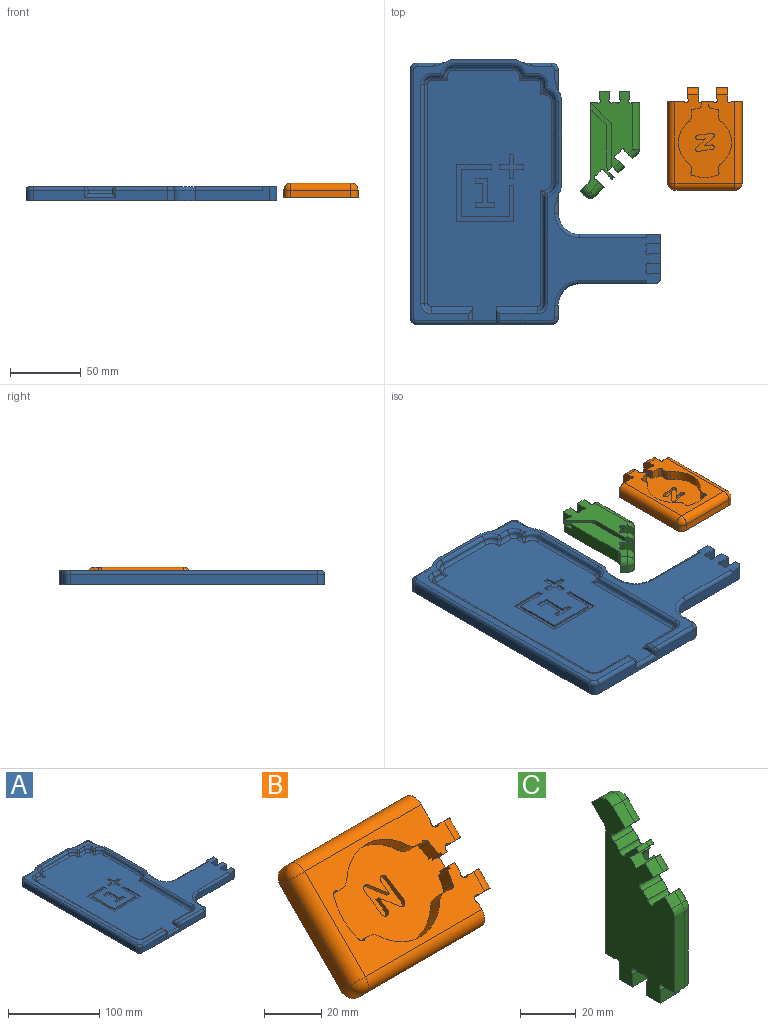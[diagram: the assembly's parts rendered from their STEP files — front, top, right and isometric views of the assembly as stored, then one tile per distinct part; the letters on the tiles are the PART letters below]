
ASSEMBLY  parts=3 mates=2
PART A: 154 faces, bbox 177.9x188.2x15 mm
  f0: plane 177.5x87.5mm, normal (0,0,1), area 13203.5mm2, adj f10,f11,f28,f29,f30,f31,f32,f33
  f1: plane 185x175mm, normal (0,0,1), area 4611.4mm2, adj f2,f3,f4,f5,f6,f7,f8,f9
  f2: plane 8x2.66mm, normal (1,0,0), area 21.3mm2, adj f1,f27,f116,f117
  f3: plane 8x7.83mm, normal (0,-1,0), area 62.6mm2, adj f1,f8,f27,f117
  f4: plane 8x7.83mm, normal (0,1,0), area 62.6mm2, adj f1,f8,f27,f116
  f5: plane 8x2.66mm, normal (1,0,0), area 21.3mm2, adj f1,f26,f114,f115
  f6: plane 8x7.83mm, normal (0,-1,0), area 62.6mm2, adj f1,f8,f26,f115
  f7: plane 8x7.83mm, normal (0,1,0), area 62.6mm2, adj f1,f8,f26,f114
  f8: plane 30x10mm, normal (1,0,0), area 185.6mm2, adj f1,f3,f4,f6,f7,f21,f25,f26
  f9: cylinder r=2.5mm len=47.5mm, axis (-1,0,0), area 186.5mm2, adj f1,f20,f80,f112
  f10: cylinder r=2.5mm len=80mm, axis (0,1,0), area 302.2mm2, adj f0,f12,f34,f60,f66
  f11: cylinder r=2.5mm len=12.5mm, axis (-1,0,0), area 37.2mm2, adj f0,f13,f38,f65,f73
  f12: cylinder r=2.5mm len=75.32mm, axis (0,-1,0), area 295.8mm2, adj f1,f10,f41,f67
  f13: cylinder r=2.5mm len=7.82mm, axis (1,0,0), area 30.7mm2, adj f1,f11,f43,f74
  f14: plane 13.49x7.5mm, normal (1,0,0), area 101.1mm2, adj f25,f95,f100,f106
  f15: plane 17.24x7.5mm, normal (0,1,0), area 129.3mm2, adj f25,f87,f102,f108
  f16: plane 95x7.5mm, normal (0,-1,0), area 602.5mm2, adj f25,f82,f84,f85,f86,f90,f96,f98
  f17: plane 175x7.5mm, normal (-1,0,0), area 1312.5mm2, adj f25,f89,f96,f102
  f18: plane 8.75x7.5mm, normal (1,0,0), area 65.6mm2, adj f19,f25,f81,f98
  f19: cylinder r=15mm len=15mm, axis (0,0,-1), area 176.7mm2, adj f18,f20,f25,f80
  f20: plane 52.5x10mm, normal (0,-1,0), area 406.2mm2, adj f1,f9,f19,f25,f112,f118
  f21: plane 57.5x10mm, normal (0,1,0), area 456.2mm2, adj f1,f8,f22,f25,f91,f113
  f22: cylinder r=15mm len=15mm, axis (0,0,-1), area 176.7mm2, adj f21,f23,f25,f92
  f23: plane 12.24x7.5mm, normal (1,0,0), area 91.8mm2, adj f22,f25,f93,f104
  f24: plane 18.49x7.5mm, normal (0,1,0), area 138.6mm2, adj f25,f94,f100,f110
  f25: plane 187.5x177.5mm, normal (0,0,-1), area 22331mm2, adj f8,f14,f15,f16,f17,f18,f19,f20
  f26: plane 10.54x8.08mm, normal (0,0,1), area 74.9mm2, adj f5,f6,f7,f8,f114,f115
  f27: plane 10.54x8.08mm, normal (0,0,1), area 74.9mm2, adj f2,f3,f4,f8,f116,f117
  f28: plane 10x2.5mm, normal (1,0,0), area 20.1mm2, adj f0,f30,f46,f86
  f29: plane 10x2.5mm, normal (-1,0,0), area 20.1mm2, adj f0,f32,f39,f84
  f30: cylinder r=2.5mm len=29mm, axis (1,0,0), area 113.9mm2, adj f0,f28,f31,f48
  f31: torus R=2.5mm, axis (0,0,1), area 25.2mm2, adj f0,f30,f33,f49
  f32: cylinder r=2.5mm len=29mm, axis (1,0,0), area 113.9mm2, adj f0,f29,f34,f40
  f33: cylinder r=2.5mm len=155mm, axis (0,-1,0), area 608.7mm2, adj f0,f31,f35,f47
  f34: torus R=2.5mm, axis (0,0,1), area 25.2mm2, adj f0,f10,f32,f41
  f35: torus R=2.5mm, axis (0,0,1), area 25.2mm2, adj f0,f33,f37,f45
  f36: cylinder r=2.5mm len=7.5mm, axis (0,1,0), area 17.5mm2, adj f0,f38,f42,f56,f71
  f37: cylinder r=2.5mm len=11.25mm, axis (-1,0,0), area 32.3mm2, adj f0,f35,f44,f61,f78
  f38: torus R=2.5mm, axis (0,0,1), area 25.2mm2, adj f0,f11,f36,f43
  f39: cylinder r=2.5mm len=7.5mm, axis (0,-1,0), area 24.5mm2, adj f1,f29,f40,f83
  f40: cylinder r=2.5mm len=29mm, axis (-1,0,0), area 109mm2, adj f1,f32,f39,f41
  f41: torus R=7.5mm, axis (0,0,1), area 36.4mm2, adj f1,f12,f34,f40
  f42: cylinder r=2.5mm len=2.82mm, axis (0,-1,0), area 11.1mm2, adj f1,f36,f43,f72
  f43: torus R=7.5mm, axis (0,0,1), area 36.4mm2, adj f1,f13,f38,f42
  f44: cylinder r=2.5mm len=6.57mm, axis (1,0,0), area 25.8mm2, adj f1,f37,f45,f79
  f45: torus R=7.5mm, axis (0,0,1), area 36.4mm2, adj f1,f35,f44,f47
  f46: cylinder r=2.5mm len=7.5mm, axis (0,1,0), area 24.5mm2, adj f1,f28,f48,f88
  f47: cylinder r=2.5mm len=155mm, axis (0,1,0), area 608.7mm2, adj f1,f33,f45,f49
  f48: cylinder r=2.5mm len=29mm, axis (-1,0,0), area 109mm2, adj f1,f30,f46,f49
  f49: torus R=7.5mm, axis (0,0,1), area 36.4mm2, adj f1,f31,f47,f48
  f50: cylinder r=12.5mm len=10mm, axis (0,0,1), area 68.4mm2, adj f1,f25,f51,f108,f109
  f51: plane 41.25x10mm, normal (0,1,0), area 412.5mm2, adj f1,f25,f50,f52
  f52: cylinder r=12.5mm len=10mm, axis (0,0,1), area 68.4mm2, adj f1,f25,f51,f110,f111
  f53: plane 57.5x10mm, normal (1,0,0), area 575mm2, adj f1,f25,f54,f55
  f54: cylinder r=12.5mm len=10mm, axis (0,0,1), area 68.4mm2, adj f1,f25,f53,f104,f105
  f55: cylinder r=12.5mm len=10mm, axis (0,0,1), area 68.4mm2, adj f1,f25,f53,f106,f107
  f56: cylinder r=2.5mm len=2.5mm, axis (1,0,0), area 1.8mm2, adj f0,f36,f57,f71
  f57: torus R=5mm, axis (0,0,1), area 38.3mm2, adj f0,f56,f58,f70,f71
  f58: cylinder r=2.5mm len=57.5mm, axis (0,-1,0), area 225.8mm2, adj f0,f57,f59,f69
  f59: torus R=5mm, axis (0,0,1), area 38.3mm2, adj f0,f58,f60,f66,f68
  f60: cylinder r=2.5mm len=2.5mm, axis (-1,0,0), area 1.8mm2, adj f0,f10,f59,f66
  f61: cylinder r=2.5mm len=2.5mm, axis (0,1,0), area 1.8mm2, adj f0,f37,f62,f78
  f62: torus R=5mm, axis (0,0,1), area 38.3mm2, adj f0,f61,f63,f77,f78
  f63: cylinder r=2.5mm len=41.25mm, axis (1,0,0), area 162mm2, adj f0,f62,f64,f76
  f64: torus R=5mm, axis (0,0,1), area 38.3mm2, adj f0,f63,f65,f73,f75
  f65: cylinder r=2.5mm len=2.5mm, axis (0,-1,0), area 1.8mm2, adj f0,f11,f64,f73
  f66: bspline ~4.92x4.19mm, area 9.5mm2, adj f10,f59,f60,f67
  f67: sphere r=2.5mm, area 12.2mm2, adj f12,f66,f68
  f68: torus R=10mm, axis (0,0,1), area 43.5mm2, adj f1,f59,f67,f69
  f69: cylinder r=2.5mm len=57.5mm, axis (0,-1,0), area 225.8mm2, adj f1,f58,f68,f70
  f70: torus R=10mm, axis (0,0,1), area 43.5mm2, adj f1,f57,f69,f72
  f71: bspline ~4.92x4.19mm, area 9.5mm2, adj f36,f56,f57,f72
  f72: sphere r=2.5mm, area 12.2mm2, adj f42,f70,f71
  f73: bspline ~4.92x4.19mm, area 9.5mm2, adj f11,f64,f65,f74
  f74: sphere r=2.5mm, area 12.2mm2, adj f13,f73,f75
  f75: torus R=10mm, axis (0,0,1), area 43.5mm2, adj f1,f64,f74,f76
  f76: cylinder r=2.5mm len=41.25mm, axis (1,0,0), area 162mm2, adj f1,f63,f75,f77
  f77: torus R=10mm, axis (0,0,1), area 43.5mm2, adj f1,f62,f76,f79
  f78: bspline ~4.92x4.19mm, area 9.5mm2, adj f37,f61,f62,f79
  f79: sphere r=2.5mm, area 12.2mm2, adj f44,f77,f78
  f80: torus R=17.5mm, axis (0,0,1), area 98.1mm2, adj f1,f9,f19,f81
  f81: cylinder r=2.5mm len=8.75mm, axis (0,-1,0), area 34.4mm2, adj f1,f18,f80,f99
  f82: cylinder r=2.5mm len=36.5mm, axis (-1,0,0), area 143.3mm2, adj f1,f16,f83,f99
  f83: sphere r=2.5mm, area 9.8mm2, adj f39,f82,f84
  f84: cylinder r=2.5mm len=5mm, axis (0,0,1), area 14.7mm2, adj f16,f29,f83,f85
  f85: cylinder r=2.5mm len=22mm, axis (-1,0,0), area 76.6mm2, adj f0,f16,f84,f86
  f86: cylinder r=2.5mm len=5mm, axis (0,0,-1), area 14.7mm2, adj f16,f28,f85,f88
  f87: cylinder r=2.5mm len=17.24mm, axis (1,0,0), area 54.3mm2, adj f1,f15,f103,f109
  f88: sphere r=2.5mm, area 13.4mm2, adj f46,f86,f90
  f89: cylinder r=2.5mm len=175mm, axis (0,1,0), area 687.2mm2, adj f1,f17,f97,f103
  f90: cylinder r=2.5mm len=36.5mm, axis (-1,0,0), area 143.3mm2, adj f1,f16,f88,f97
  f91: cylinder r=2.5mm len=47.5mm, axis (1,0,0), area 186.5mm2, adj f1,f21,f92,f113
  f92: torus R=17.5mm, axis (0,0,1), area 98.1mm2, adj f1,f22,f91,f93
  f93: cylinder r=2.5mm len=12.24mm, axis (0,-1,0), area 34.7mm2, adj f1,f23,f92,f105
  f94: cylinder r=2.5mm len=18.49mm, axis (1,0,0), area 59.2mm2, adj f1,f24,f101,f111
  f95: cylinder r=2.5mm len=13.49mm, axis (0,-1,0), area 39.6mm2, adj f1,f14,f101,f107
  f96: cylinder r=5mm len=7.5mm, axis (0,0,-1), area 58.9mm2, adj f16,f17,f25,f97
  f97: torus R=2.5mm, axis (0,0,1), area 25.2mm2, adj f1,f89,f90,f96
  f98: cylinder r=5mm len=7.5mm, axis (0,0,1), area 58.9mm2, adj f16,f18,f25,f99
  f99: torus R=2.5mm, axis (0,0,1), area 25.2mm2, adj f1,f81,f82,f98
  f100: cylinder r=5mm len=7.5mm, axis (0,0,-1), area 58.9mm2, adj f14,f24,f25,f101
  f101: torus R=2.5mm, axis (0,0,1), area 25.2mm2, adj f1,f94,f95,f100
  f102: cylinder r=5mm len=7.5mm, axis (0,0,1), area 58.9mm2, adj f15,f17,f25,f103
  f103: torus R=2.5mm, axis (0,0,1), area 25.2mm2, adj f1,f87,f89,f102
  f104: cylinder r=5mm len=7.5mm, axis (0,0,1), area 20.3mm2, adj f23,f25,f54,f105
  f105: bspline ~9.82x7.96mm, area 13.2mm2, adj f1,f54,f93,f104
  f106: cylinder r=5mm len=7.5mm, axis (0,0,1), area 20.3mm2, adj f14,f25,f55,f107
  f107: bspline ~9.82x7.96mm, area 13.2mm2, adj f1,f55,f95,f106
  f108: cylinder r=5mm len=7.5mm, axis (0,0,1), area 20.3mm2, adj f15,f25,f50,f109
  f109: bspline ~9.82x7.96mm, area 13.2mm2, adj f1,f50,f87,f108
  f110: cylinder r=5mm len=7.5mm, axis (0,0,1), area 20.3mm2, adj f24,f25,f52,f111
  f111: bspline ~9.82x7.96mm, area 13.2mm2, adj f1,f52,f94,f110
  f112: plane 2.5x2.5mm, normal (-1,0,0), area 1.3mm2, adj f1,f9,f20
  f113: plane 2.5x2.5mm, normal (-1,0,0), area 1.3mm2, adj f1,f21,f91
  f114: cylinder r=1.59mm len=8mm, axis (0,0,-1), area 39.9mm2, adj f1,f5,f7,f26
  f115: cylinder r=1.59mm len=8mm, axis (0,0,-1), area 39.9mm2, adj f1,f5,f6,f26
  f116: cylinder r=1.59mm len=8mm, axis (0,0,-1), area 39.9mm2, adj f1,f2,f4,f27
  f117: cylinder r=1.59mm len=8mm, axis (0,0,-1), area 39.9mm2, adj f1,f2,f3,f27
  f118: cylinder r=5mm len=10mm, axis (0,0,-1), area 78.5mm2, adj f1,f8,f20,f25
  f119: plane 24.75x1.5mm, normal (0,-1,0), area 37.1mm2, adj f0,f120,f128,f129
  f120: plane 40.5x1.5mm, normal (1,0,0), area 60.8mm2, adj f0,f119,f121,f129
  f121: plane 40.5x1.5mm, normal (0,1,0), area 60.7mm2, adj f0,f120,f122,f129
  f122: plane 25.31x1.5mm, normal (-1,0,0), area 38mm2, adj f0,f121,f123,f129
  f123: plane 3.38x1.5mm, normal (0,-1,0), area 5.1mm2, adj f0,f122,f124,f129
  f124: plane 21.94x1.5mm, normal (1,0,0), area 32.9mm2, adj f0,f123,f125,f129
  f125: plane 33.75x1.5mm, normal (0,-1,0), area 50.6mm2, adj f0,f124,f126,f129
  f126: plane 33.75x1.5mm, normal (-1,0,0), area 50.6mm2, adj f0,f125,f127,f129
  f127: plane 21.38x1.5mm, normal (0,1,0), area 32.1mm2, adj f0,f126,f128,f129
  f128: plane 3.38x1.5mm, normal (-1,0,0), area 5.1mm2, adj f0,f119,f127,f129
  f129: plane 40.5x40.5mm, normal (0,0,1), area 408.2mm2, adj f119,f120,f121,f122,f123,f124,f125,f126
  f130: plane 8.44x1.5mm, normal (0,-1,0), area 12.7mm2, adj f0,f131,f139,f140
  f131: plane 3.38x1.5mm, normal (1,0,0), area 5.1mm2, adj f0,f130,f132,f140
  f132: plane 5.06x1.5mm, normal (0,1,0), area 7.6mm2, adj f0,f131,f133,f140
  f133: plane 13.5x1.5mm, normal (1,0,0), area 20.3mm2, adj f0,f132,f134,f140
  f134: plane 5.06x1.5mm, normal (0,-1,0), area 7.6mm2, adj f0,f133,f135,f140
  f135: plane 3.38x1.5mm, normal (1,0,0), area 5.1mm2, adj f0,f134,f136,f140
  f136: plane 13.5x1.5mm, normal (0,1,0), area 20.3mm2, adj f0,f135,f137,f140
  f137: plane 3.38x1.5mm, normal (-1,0,0), area 5.1mm2, adj f0,f136,f138,f140
  f138: plane 5.06x1.5mm, normal (0,-1,0), area 7.6mm2, adj f0,f137,f139,f140
  f139: plane 16.88x1.5mm, normal (-1,0,0), area 25.3mm2, adj f0,f130,f138,f140
  f140: plane 20.25x13.5mm, normal (0,0,1), area 119.6mm2, adj f130,f131,f132,f133,f134,f135,f136,f137
  f141: plane 6.75x1.5mm, normal (-1,0,0), area 10.1mm2, adj f0,f142,f152,f153
  f142: plane 3.38x1.5mm, normal (0,-1,0), area 5.1mm2, adj f0,f141,f143,f153
  f143: plane 6.75x1.5mm, normal (1,0,0), area 10.1mm2, adj f0,f142,f144,f153
  f144: plane 6.75x1.5mm, normal (0,-1,0), area 10.1mm2, adj f0,f143,f145,f153
  f145: plane 3.38x1.5mm, normal (1,0,0), area 5.1mm2, adj f0,f144,f146,f153
  f146: plane 6.75x1.5mm, normal (0,1,0), area 10.1mm2, adj f0,f145,f147,f153
  f147: plane 6.75x1.5mm, normal (1,0,0), area 10.1mm2, adj f0,f146,f148,f153
  f148: plane 3.38x1.5mm, normal (0,1,0), area 5.1mm2, adj f0,f147,f149,f153
  f149: plane 6.75x1.5mm, normal (-1,0,0), area 10.1mm2, adj f0,f148,f150,f153
  f150: plane 6.75x1.5mm, normal (0,1,0), area 10.1mm2, adj f0,f149,f151,f153
  f151: plane 3.38x1.5mm, normal (-1,0,0), area 5.1mm2, adj f0,f150,f152,f153
  f152: plane 6.75x1.5mm, normal (0,-1,0), area 10.1mm2, adj f0,f141,f151,f153
  f153: plane 16.88x16.88mm, normal (0,0,1), area 102.5mm2, adj f141,f142,f143,f144,f145,f146,f147,f148
PART B: 62 faces, bbox 72.5x42.1x42.1 mm
  f0: plane 62.5x30mm, normal (0,-0.71,0.71), area 1144.2mm2, adj f1,f2,f3,f4,f5,f6,f7,f8
  f1: plane 4.6x4.6mm, normal (0,0.71,0.71), area 13.7mm2, adj f0,f31,f40,f50
  f2: cylinder r=24.75mm len=7.91mm, axis (0,-0.71,0.71), area 31.3mm2, adj f0,f31,f41,f50
  f3: cylinder r=24.75mm len=16.33mm, axis (0,-0.71,0.71), area 110mm2, adj f0,f31,f48,f49
  f4: plane 4.6x4.6mm, normal (0,0.71,0.71), area 11.7mm2, adj f0,f31,f38,f49
  f5: plane 4.6x4.6mm, normal (0,-0.71,-0.71), area 11.7mm2, adj f0,f31,f37,f48
  f6: cylinder r=24.75mm len=7.91mm, axis (0,-0.71,0.71), area 31.3mm2, adj f0,f31,f34,f47
  f7: plane 4.6x4.6mm, normal (0,-0.71,-0.71), area 13.7mm2, adj f0,f31,f35,f47
  f8: plane 12.56x10.48mm, normal (1,0,0), area 72.2mm2, adj f0,f16,f22,f23,f46
  f9: plane 7.76x7.07mm, normal (0,-0.71,-0.71), area 72.2mm2, adj f0,f16,f17,f30,f46
  f10: plane 12.84x9.81mm, normal (1,0,0), area 53.7mm2, adj f0,f16,f31,f32,f44,f45
  f11: plane 7.76x7.07mm, normal (0,0.71,0.71), area 72.2mm2, adj f0,f16,f17,f30,f45
  f12: plane 4.6x4.6mm, normal (0,-0.71,-0.71), area 18.4mm2, adj f0,f31,f33,f44
  f13: plane 7.76x7.07mm, normal (0,-0.71,-0.71), area 72.2mm2, adj f0,f16,f18,f29,f44
  f14: plane 15.44x13.37mm, normal (1,0,0), area 112.9mm2, adj f0,f16,f19,f21,f43
  f15: plane 7.76x7.07mm, normal (0,0.71,0.71), area 72.2mm2, adj f0,f16,f18,f29,f43
  f16: plane 72.5x37.07mm, normal (0,0.71,-0.71), area 3417.2mm2, adj f8,f9,f10,f11,f13,f14,f15,f17
  f17: plane 9.09x9.09mm, normal (1,0,0), area 39.2mm2, adj f9,f11,f16,f30
  f18: plane 9.09x9.09mm, normal (1,0,0), area 39.2mm2, adj f13,f15,f16,f29
  f19: plane 57.5x3.54mm, normal (0,0.71,0.71), area 287.5mm2, adj f14,f16,f21,f28
  f20: plane 33.54x33.54mm, normal (-1,0,0), area 212.1mm2, adj f16,f24,f26,f28
  f21: cylinder r=5mm len=57.5mm, axis (-1,0,0), area 451.6mm2, adj f0,f14,f19,f27
  f22: plane 57.5x3.54mm, normal (0,-0.71,-0.71), area 287.5mm2, adj f8,f16,f23,f24
  f23: cylinder r=5mm len=57.5mm, axis (1,0,0), area 451.6mm2, adj f0,f8,f22,f25
  f24: cylinder r=5mm len=7.07mm, axis (0,0.71,-0.71), area 39.3mm2, adj f16,f20,f22,f25
  f25: sphere r=5mm, area 39.3mm2, adj f23,f24,f26
  f26: cylinder r=5mm len=33.54mm, axis (0,-0.71,-0.71), area 333.2mm2, adj f0,f20,f25,f27
  f27: sphere r=5mm, area 39.3mm2, adj f21,f26,f28
  f28: cylinder r=5mm len=7.07mm, axis (0,-0.71,0.71), area 39.3mm2, adj f16,f19,f20,f27
  f29: cylinder r=5mm len=9.09mm, axis (0,0.71,0.71), area 61.7mm2, adj f0,f13,f15,f18
  f30: cylinder r=5mm len=9.09mm, axis (0,0.71,0.71), area 61.7mm2, adj f0,f9,f11,f17
  f31: plane 53.5x26.52mm, normal (0,-0.71,0.71), area 1261.3mm2, adj f1,f2,f3,f4,f5,f6,f7,f10
  f32: plane 4.6x4.6mm, normal (0,0.71,0.71), area 19.5mm2, adj f0,f10,f31,f42
  f33: plane 5.3x5.3mm, normal (-1,0,0), area 6.5mm2, adj f0,f12,f31,f34
  f34: plane 4.6x4.6mm, normal (0,-0.71,-0.71), area 7.9mm2, adj f0,f6,f31,f33
  f35: cylinder r=5mm len=5.97mm, axis (0,-0.71,0.71), area 29.7mm2, adj f0,f7,f31,f36
  f36: cylinder r=18.75mm len=29.7mm, axis (0,-0.71,0.71), area 222.8mm2, adj f0,f31,f35,f37
  f37: cylinder r=5mm len=5.97mm, axis (0,-0.71,0.71), area 29.7mm2, adj f0,f5,f31,f36
  f38: cylinder r=5mm len=5.97mm, axis (0,-0.71,0.71), area 29.7mm2, adj f0,f4,f31,f39
  f39: cylinder r=18.75mm len=29.7mm, axis (0,-0.71,0.71), area 222.8mm2, adj f0,f31,f38,f40
  f40: cylinder r=5mm len=5.97mm, axis (0,-0.71,0.71), area 29.7mm2, adj f0,f1,f31,f39
  f41: plane 4.6x4.6mm, normal (0,0.71,0.71), area 7.9mm2, adj f0,f2,f31,f42
  f42: plane 5.3x5.3mm, normal (-1,0,0), area 6.5mm2, adj f0,f31,f32,f41
  f43: cylinder r=1.59mm len=8.99mm, axis (0,0.71,-0.71), area 49.9mm2, adj f0,f14,f15,f16
  f44: cylinder r=1.59mm len=8.99mm, axis (0,0.71,-0.71), area 48.1mm2, adj f0,f10,f12,f13,f16,f31
  f45: cylinder r=1.59mm len=8.99mm, axis (0,0.71,-0.71), area 49.9mm2, adj f0,f10,f11,f16
  f46: cylinder r=1.59mm len=8.99mm, axis (0,0.71,-0.71), area 49.9mm2, adj f0,f8,f9,f16
  f47: cylinder r=1.59mm len=5.94mm, axis (0,0.71,-0.71), area 25mm2, adj f0,f6,f7,f31
  f48: cylinder r=1.59mm len=5.77mm, axis (0,0.71,-0.71), area 24.8mm2, adj f0,f3,f5,f31
  f49: cylinder r=1.59mm len=5.77mm, axis (0,0.71,-0.71), area 24.8mm2, adj f0,f3,f4,f31
  f50: cylinder r=1.59mm len=5.94mm, axis (0,0.71,-0.71), area 25mm2, adj f0,f1,f2,f31
  f51: plane 4.97x4.97mm, normal (0.99,0.1,0.1), area 10.2mm2, adj f31,f52,f60,f61
  f52: plane 6.14x5.91mm, normal (-0.72,-0.49,-0.49), area 17.7mm2, adj f31,f51,f53,f61
  f53: cylinder r=1.6mm len=2.75mm, axis (0,-0.71,0.71), area 8mm2, adj f31,f52,f54,f61
  f54: plane 8.42x8.42mm, normal (0.99,0.1,0.1), area 20mm2, adj f31,f53,f55,f61
  f55: cylinder r=1.6mm len=3.18mm, axis (0,-0.71,0.71), area 10.1mm2, adj f31,f54,f56,f61
  f56: plane 4.97x4.97mm, normal (-0.99,-0.1,-0.1), area 10.2mm2, adj f31,f55,f57,f61
  f57: plane 6.14x5.91mm, normal (0.72,0.49,0.49), area 17.7mm2, adj f31,f56,f58,f61
  f58: cylinder r=1.6mm len=2.75mm, axis (0,-0.71,0.71), area 8mm2, adj f31,f57,f59,f61
  f59: plane 8.42x8.42mm, normal (-0.99,-0.1,-0.1), area 20mm2, adj f31,f58,f60,f61
  f60: cylinder r=1.6mm len=3.18mm, axis (0,-0.71,0.71), area 10.1mm2, adj f31,f51,f59,f61
  f61: plane 12.76x9.27mm, normal (0,-0.71,0.71), area 106.8mm2, adj f51,f52,f53,f54,f55,f56,f57,f58
PART C: 57 faces, bbox 10x42.1x75.9 mm
  f0: plane 5x4.22mm, normal (0,-0.71,0.71), area 29.8mm2, adj f3,f4,f14,f37
  f1: plane 54.34x30mm, normal (1,0,0), area 774.9mm2, adj f3,f5,f6,f7,f8,f9,f10,f11
  f2: plane 56.99x16.94mm, normal (1,0,0), area 523.7mm2, adj f15,f16,f17,f22,f24,f28,f30,f32
  f3: cylinder r=5mm len=7.75mm, axis (0,-0.71,-0.71), area 46.8mm2, adj f0,f1,f14,f37
  f4: plane 75.93x42.07mm, normal (-1,0,0), area 1788mm2, adj f0,f5,f6,f7,f8,f9,f10,f11
  f5: plane 10x4.58mm, normal (0,0,-1), area 45.8mm2, adj f1,f4,f24,f42,f56
  f6: plane 10x5.76mm, normal (0,1,0), area 57.5mm2, adj f1,f4,f20,f56
  f7: plane 10x2.66mm, normal (0,0,-1), area 26.6mm2, adj f1,f4,f54,f55
  f8: plane 10x5.76mm, normal (0,-1,0), area 57.5mm2, adj f1,f4,f20,f55
  f9: plane 10x5.76mm, normal (0,1,0), area 57.5mm2, adj f1,f4,f19,f54
  f10: plane 10x5.08mm, normal (0,0,-1), area 45.4mm2, adj f1,f4,f23,f35,f53
  f11: plane 10x5.76mm, normal (0,-1,0), area 57.5mm2, adj f1,f4,f19,f53
  f12: plane 10x2.59mm, normal (0,-0.71,0.71), area 36.6mm2, adj f1,f4,f51,f52
  f13: plane 10x5.48mm, normal (0,0.71,0.71), area 72.2mm2, adj f1,f4,f25,f33,f52
  f14: plane 10x5.48mm, normal (0,-0.71,-0.71), area 72.2mm2, adj f0,f1,f3,f4,f51
  f15: plane 10x2.59mm, normal (0,-0.71,0.71), area 36.6mm2, adj f2,f4,f49,f50
  f16: plane 10x5.48mm, normal (0,0.71,0.71), area 72.2mm2, adj f2,f4,f21,f22,f50
  f17: plane 10x5.48mm, normal (0,-0.71,-0.71), area 72.2mm2, adj f2,f4,f18,f30,f49
  f18: plane 6.31x6.31mm, normal (0,-0.71,0.71), area 44.6mm2, adj f4,f17,f27,f30
  f19: plane 10x6.85mm, normal (0,0,-1), area 68.5mm2, adj f1,f4,f9,f11
  f20: plane 10x6.85mm, normal (0,0,-1), area 68.5mm2, adj f1,f4,f6,f8
  f21: plane 5x1.34mm, normal (0,-0.71,0.71), area 9.4mm2, adj f4,f16,f22,f38
  f22: cylinder r=5mm len=5mm, axis (0,-0.71,-0.71), area 14.8mm2, adj f2,f16,f21,f38
  f23: plane 32.93x5mm, normal (0,-1,0), area 164.6mm2, adj f4,f10,f26,f35
  f24: plane 53.79x10mm, normal (0,1,0), area 506.6mm2, adj f2,f4,f5,f36,f43,f48
  f25: plane 5x3.43mm, normal (0,-0.71,0.71), area 24.3mm2, adj f4,f13,f26,f33
  f26: cylinder r=5mm len=5mm, axis (-1,0,0), area 19.6mm2, adj f4,f23,f25,f34
  f27: cylinder r=5mm len=7.07mm, axis (-1,0,0), area 39.3mm2, adj f4,f18,f29,f31
  f28: plane 10x5.61mm, normal (0,0.71,-0.71), area 73.9mm2, adj f2,f4,f29,f32,f36
  f29: plane 5x3.54mm, normal (0,0.71,0.71), area 25mm2, adj f4,f27,f28,f32
  f30: cylinder r=5mm len=9.85mm, axis (0,-0.71,-0.71), area 70.1mm2, adj f2,f17,f18,f31
  f31: sphere r=5mm, area 39.3mm2, adj f27,f30,f32
  f32: cylinder r=5mm len=7.07mm, axis (0,0.71,-0.71), area 39.3mm2, adj f2,f28,f29,f31
  f33: cylinder r=5mm len=6.97mm, axis (0,-0.71,-0.71), area 38.1mm2, adj f1,f13,f25,f34
  f34: sphere r=5mm, area 19.6mm2, adj f26,f33,f35
  f35: cylinder r=5mm len=32.93mm, axis (0,0,-1), area 258.6mm2, adj f1,f10,f23,f34
  f36: cylinder r=5mm len=10mm, axis (1,0,0), area 39.3mm2, adj f2,f4,f24,f28
  f37: plane 10x4.6mm, normal (0,0.71,0.71), area 59.6mm2, adj f0,f1,f3,f4,f39
  f38: plane 10x4.6mm, normal (0,-0.71,-0.71), area 59.6mm2, adj f2,f4,f21,f22,f39
  f39: plane 10x3.18mm, normal (0,-0.71,0.71), area 30.6mm2, adj f1,f2,f4,f37,f38,f40,f47,f48
  f40: plane 29.34x4.5mm, normal (0,1,0), area 132mm2, adj f1,f39,f41,f48
  f41: cylinder r=3.2mm len=4.5mm, axis (1,0,0), area 11.3mm2, adj f1,f40,f42,f48
  f42: plane 14.13x14.13mm, normal (0,0.71,0.71), area 89.9mm2, adj f1,f5,f41,f48
  f43: cylinder r=1mm len=4.5mm, axis (1,0,0), area 10.6mm2, adj f2,f24,f44,f48
  f44: plane 9.58x9.58mm, normal (0,-0.71,-0.71), area 61mm2, adj f2,f43,f45,f48
  f45: cylinder r=2mm len=4.5mm, axis (1,0,0), area 7.1mm2, adj f2,f44,f46,f48
  f46: plane 28.51x4.5mm, normal (0,-1,0), area 128.3mm2, adj f2,f45,f47,f48
  f47: cylinder r=3.2mm len=4.5mm, axis (1,0,0), area 11.3mm2, adj f2,f39,f46,f48
  f48: plane 48x15.07mm, normal (1,0,0), area 162.1mm2, adj f24,f39,f40,f41,f42,f43,f44,f45
  f49: cylinder r=1.59mm len=10mm, axis (-1,0,0), area 49.9mm2, adj f2,f4,f15,f17
  f50: cylinder r=1.59mm len=10mm, axis (-1,0,0), area 49.9mm2, adj f2,f4,f15,f16
  f51: cylinder r=1.59mm len=10mm, axis (-1,0,0), area 49.9mm2, adj f1,f4,f12,f14
  f52: cylinder r=1.59mm len=10mm, axis (-1,0,0), area 49.9mm2, adj f1,f4,f12,f13
  f53: cylinder r=1.59mm len=10mm, axis (-1,0,0), area 49.9mm2, adj f1,f4,f10,f11
  f54: cylinder r=1.59mm len=10mm, axis (-1,0,0), area 49.9mm2, adj f1,f4,f7,f9
  f55: cylinder r=1.59mm len=10mm, axis (-1,0,0), area 49.9mm2, adj f1,f4,f7,f8
  f56: cylinder r=1.59mm len=10mm, axis (-1,0,0), area 49.9mm2, adj f1,f4,f5,f6
PLACE A t=(-10.7,4.62,0)mm
PLACE B rot(axis=(-0.36,-0.36,0.86),98.4deg) t=(155.54,-45.38,-64.4)mm
PLACE C rot(axis=(0.58,-0.58,0.58),120deg) t=(35.55,79.21,-114.83)mm
MATE parallel C.f24 <-> A.f53  axis (-1,0,0) through (64.3,40.87,5)mm
MATE parallel A.f53 <-> B.f19  axis (1,0,0) through (44.3,40.87,5)mm
